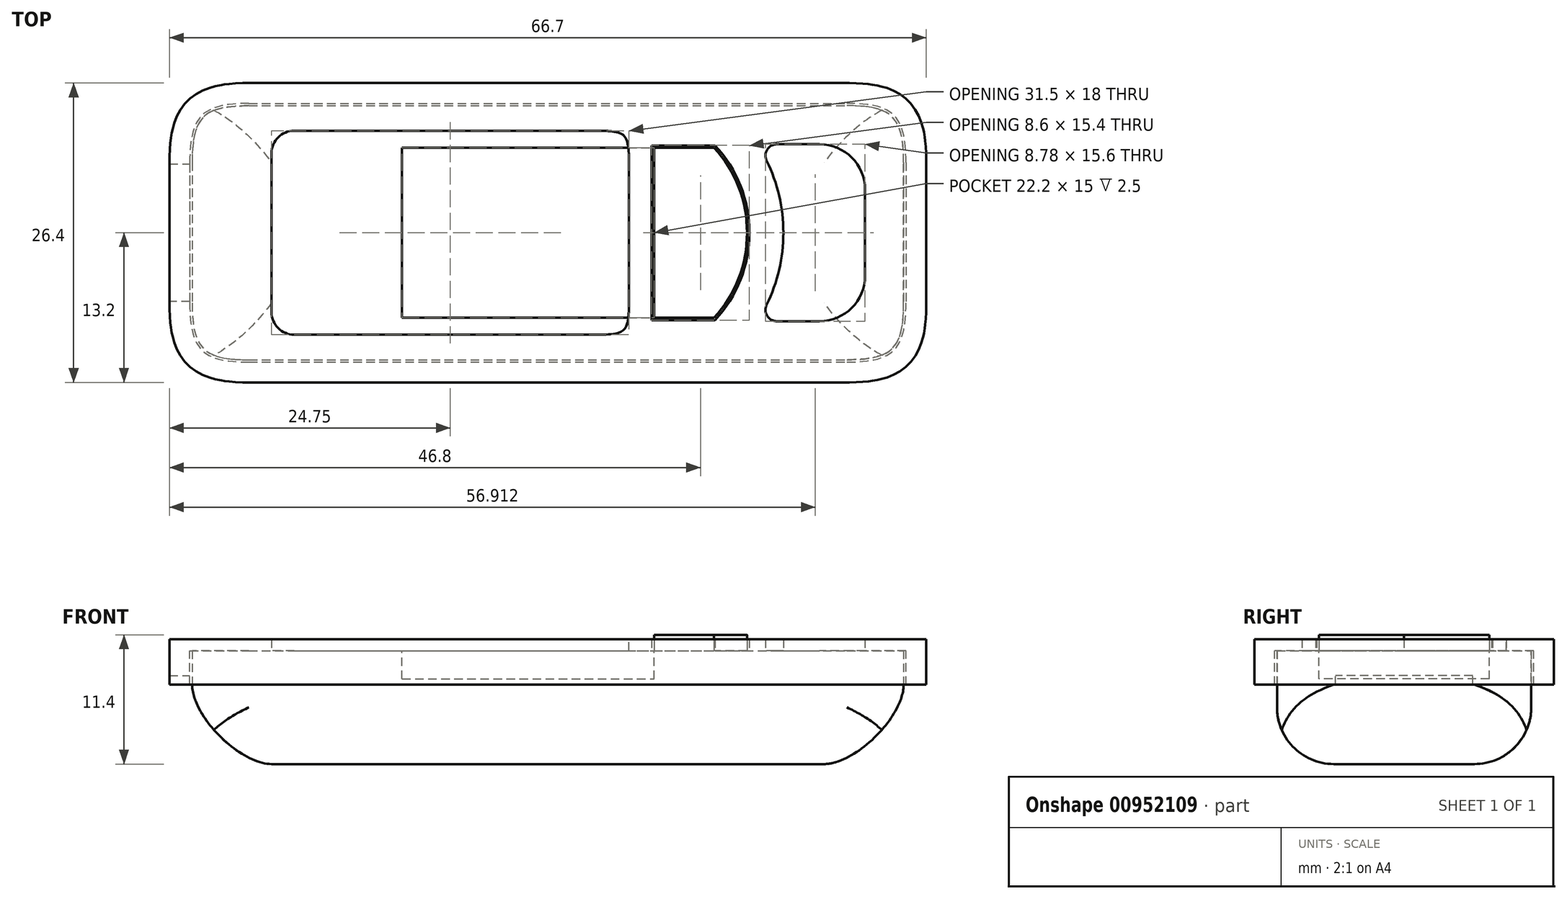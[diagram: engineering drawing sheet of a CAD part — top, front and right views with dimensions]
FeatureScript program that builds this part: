
annotation { "Feature Type Name" : "Feature", "Feature Type Description" : "" }
export const myFeature = defineFeature(function(context is Context, id is Id, definition is map)
    precondition{}
    {
        {
            var Q0;
            Q0=qCreatedBy(makeId("Top.planeOp"),FACE);
            var sketch = newSketch(context, id + "F0", { "sketchPlane" : qUnion([Q0])});
            skLineSegment(sketch, "E0.bottom", {"start": v(-27.35, 11.2) * mm, "end": v(27.35, 11.2) * mm});
            skLineSegment(sketch, "E0.top", {"start": v(-27.35, -11.2) * mm, "end": v(27.35, -11.2) * mm});
            skLineSegment(sketch, "E0.left", {"start": v(-31.35, 7.2) * mm, "end": v(-31.35, -7.2) * mm});
            skLineSegment(sketch, "E0.right", {"start": v(31.35, 7.2) * mm, "end": v(31.35, -7.2) * mm});
            skPoint(sketch, "E0.middle", {"position": v(0, 0) * mm});
            skLineSegment(sketch, "E1", {"start": v(31.35, 0) * mm, "end": v(17.55, 0) * mm, "construction": true});
            skLineSegment(sketch, "E2", {"start": v(17.55, 0) * mm, "end": v(9.35, 0) * mm, "construction": true});
            skLineSegment(sketch, "E3", {"start": v(9.35, 0) * mm, "end": v(-11.85, 0) * mm, "construction": true});
            skLineSegment(sketch, "E4", {"start": v(-11.85, 0) * mm, "end": v(-12.85, 0) * mm, "construction": true});
            skLineSegment(sketch, "E5", {"start": v(9.35, 0) * mm, "end": v(9.35, 7.5) * mm});
            skLineSegment(sketch, "E6.MirrorCS", {"start": v(9.35, 0) * mm, "end": v(9.35, -7.5) * mm});
            skLineSegment(sketch, "E7", {"start": v(9.35, 7.5) * mm, "end": v(14.65, 7.5) * mm});
            skLineSegment(sketch, "E8", {"start": v(14.65, 7.5) * mm, "end": v(14.65, 0) * mm});
            skArc(sketch, "E9", {"start": v(17.55, 0) * mm, "mid": v(16.8, 4.02) * mm, "end": v(14.65, 7.5) * mm});
            skLineSegment(sketch, "E10.MirrorCS", {"start": v(9.35, -7.5) * mm, "end": v(14.65, -7.5) * mm});
            skLineSegment(sketch, "E11.MirrorCS", {"start": v(14.65, -7.5) * mm, "end": v(14.65, 0) * mm});
            skArc(sketch, "E12.MirrorCS", {"start": v(17.55, 0) * mm, "mid": v(16.8, -4.02) * mm, "end": v(14.65, -7.5) * mm});
            skLineSegment(sketch, "E13", {"start": v(-12.85, 0) * mm, "end": v(-12.85, 7.5) * mm});
            skLineSegment(sketch, "E14", {"start": v(-12.85, 7.5) * mm, "end": v(9.35, 7.5) * mm});
            skLineSegment(sketch, "E15", {"start": v(-12.85, 0) * mm, "end": v(-12.85, -7.5) * mm});
            skLineSegment(sketch, "E16", {"start": v(-12.85, -7.5) * mm, "end": v(9.35, -7.5) * mm});
            skLineSegment(sketch, "E17", {"start": v(-31.35, 0) * mm, "end": v(-27.35, 0) * mm, "construction": true});
            skLineSegment(sketch, "E18", {"start": v(31.35, 0) * mm, "end": v(27.35, 0) * mm, "construction": true});
            skLineSegment(sketch, "E19", {"start": v(27.35, 0) * mm, "end": v(27.35, 11.2) * mm, "construction": true});
            skLineSegment(sketch, "E20", {"start": v(-27.35, 0) * mm, "end": v(-27.35, 11.2) * mm, "construction": true});
            skLineSegment(sketch, "E21.MirrorCS", {"start": v(-27.35, 0) * mm, "end": v(-27.35, -11.2) * mm, "construction": true});
            skLineSegment(sketch, "E22.MirrorCS", {"start": v(27.35, 0) * mm, "end": v(27.35, -11.2) * mm, "construction": true});
            skPoint(sketch, "E23.visualSharp", {"position": v(-31.35, 11.2) * mm});
            skArc(sketch, "E23.filletArc", {"start": v(-27.35, 11.2) * mm, "mid": v(-30.18, 10.03) * mm, "end": v(-31.35, 7.2) * mm});
            skPoint(sketch, "E24.visualSharp", {"position": v(-31.35, -11.2) * mm});
            skArc(sketch, "E24.filletArc", {"start": v(-31.35, -7.2) * mm, "mid": v(-30.18, -10.03) * mm, "end": v(-27.35, -11.2) * mm});
            skPoint(sketch, "E25.visualSharp", {"position": v(31.35, 11.2) * mm});
            skArc(sketch, "E25.filletArc", {"start": v(31.35, 7.2) * mm, "mid": v(30.18, 10.03) * mm, "end": v(27.35, 11.2) * mm});
            skPoint(sketch, "E26.visualSharp", {"position": v(31.35, -11.2) * mm});
            skArc(sketch, "E26.filletArc", {"start": v(27.35, -11.2) * mm, "mid": v(30.18, -10.03) * mm, "end": v(31.35, -7.2) * mm});
            skLineSegment(sketch, "E27", {"start": v(-27.35, 11.2) * mm, "end": v(-31.35, 11.2) * mm});
            skLineSegment(sketch, "E28", {"start": v(-31.35, 7.2) * mm, "end": v(-31.35, 11.2) * mm});
            skLineSegment(sketch, "E29.MirrorCS", {"start": v(-31.35, -7.2) * mm, "end": v(-31.35, -11.2) * mm});
            skLineSegment(sketch, "E30.MirrorCS", {"start": v(-27.35, -11.2) * mm, "end": v(-31.35, -11.2) * mm});
            skLineSegment(sketch, "E31.MirrorCS", {"start": v(27.35, 11.2) * mm, "end": v(31.35, 11.2) * mm});
            skLineSegment(sketch, "E32.MirrorCS", {"start": v(31.35, 7.2) * mm, "end": v(31.35, 11.2) * mm});
            skLineSegment(sketch, "E33.MirrorCS", {"start": v(27.35, -11.2) * mm, "end": v(31.35, -11.2) * mm});
            skLineSegment(sketch, "E34.MirrorCS", {"start": v(31.35, -7.2) * mm, "end": v(31.35, -11.2) * mm});
            skSolve(sketch);
        }
        {
            var Q0;
            Q0=makeQuery(id+"F0.imprint","IMPRINT",FACE,{"disambiguationData":[TD([[makeQuery(id+"F0.imprint","IMPRINT",EDGE,{"derivedFrom":sQuery(id+"F0.wireOp",EDGE,"E0.bottom")}),-1.0]])]});
            var Q1;
            Q1=makeQuery(id+"F0.imprint","IMPRINT",FACE,{"disambiguationData":[TD([[makeQuery(id+"F0.imprint","IMPRINT",EDGE,{"derivedFrom":sQuery(id+"F0.wireOp",EDGE,"E5")}),1.0]])]});
            var Q2;
            Q2=makeQuery(id+"F0.imprint","IMPRINT",FACE,{"disambiguationData":[TD([[makeQuery(id+"F0.imprint","IMPRINT",EDGE,{"derivedFrom":sQuery(id+"F0.wireOp",EDGE,"E5")}),-1.0]])]});
            var Q3;
            Q3=makeQuery(id+"F0.imprint","IMPRINT",FACE,{"disambiguationData":[TD([[makeQuery(id+"F0.imprint","IMPRINT",EDGE,{"derivedFrom":sQuery(id+"F0.wireOp",EDGE,"E8")}),1.0]])]});
            var Q4;
            Q4=makeQuery(id+"F0.imprint","IMPRINT",FACE,{"disambiguationData":[TD([[makeQuery(id+"F0.imprint","IMPRINT",EDGE,{"derivedFrom":sQuery(id+"F0.wireOp",EDGE,"E23.filletArc")}),-1.0]])]});
            var Q5;
            Q5=makeQuery(id+"F0.imprint","IMPRINT",FACE,{"disambiguationData":[TD([[makeQuery(id+"F0.imprint","IMPRINT",EDGE,{"derivedFrom":sQuery(id+"F0.wireOp",EDGE,"E24.filletArc")}),-1.0]])]});
            var Q6;
            Q6=makeQuery(id+"F0.imprint","IMPRINT",FACE,{"disambiguationData":[TD([[makeQuery(id+"F0.imprint","IMPRINT",EDGE,{"derivedFrom":sQuery(id+"F0.wireOp",EDGE,"E26.filletArc")}),-1.0]])]});
            var Q7;
            Q7=makeQuery(id+"F0.imprint","IMPRINT",FACE,{"disambiguationData":[TD([[makeQuery(id+"F0.imprint","IMPRINT",EDGE,{"derivedFrom":sQuery(id+"F0.wireOp",EDGE,"E25.filletArc")}),-1.0]])]});
            extrude(context, id + "F1", {"entities" : qUnion([Q0, Q1, Q2, Q3, Q4, Q5, Q6, Q7]), "oppositeDirection" : true, "depth" : 10 * mm, "offsetDistance" : 25 * mm});
        }
        {
            var Q0;
            Q0=makeQuery(id+"F0.imprint","IMPRINT",FACE,{"disambiguationData":[TD([[makeQuery(id+"F0.imprint","IMPRINT",EDGE,{"derivedFrom":sQuery(id+"F0.wireOp",EDGE,"E5")}),1.0]])]});
            extrude(context, id + "F2", {"entities" : qUnion([Q0]), "operationType" : NewBodyOperationType.REMOVE, "oppositeDirection" : true, "depth" : 2.5 * mm, "offsetDistance" : 25 * mm});
        }
        {
            var Q0;
            Q0=makeQuery(id+"F0.imprint","IMPRINT",FACE,{"disambiguationData":[TD([[makeQuery(id+"F0.imprint","IMPRINT",EDGE,{"derivedFrom":sQuery(id+"F0.wireOp",EDGE,"E5")}),-1.0]])]});
            var Q1;
            Q1=makeQuery(id+"F0.imprint","IMPRINT",FACE,{"disambiguationData":[TD([[makeQuery(id+"F0.imprint","IMPRINT",EDGE,{"derivedFrom":sQuery(id+"F0.wireOp",EDGE,"E8")}),1.0]])]});
            extrude(context, id + "F3", {"entities" : qUnion([Q0, Q1]), "operationType" : NewBodyOperationType.ADD, "depth" : 1.4 * mm, "offsetDistance" : 25 * mm});
        }
        {
            var Q0;
            Q0=makeQuery(id+"F1.opExtrude","SWEPT_EDGE",EDGE,{"disambiguationData":[OSD([sQuery(id+"F0.wireOp",EDGE,"E33.MirrorCS"),sQuery(id+"F0.wireOp",EDGE,"E34.MirrorCS")])]});
            var Q1;
            Q1=makeQuery(id+"F1.opExtrude","SWEPT_EDGE",EDGE,{"disambiguationData":[OSD([sQuery(id+"F0.wireOp",EDGE,"E31.MirrorCS"),sQuery(id+"F0.wireOp",EDGE,"E32.MirrorCS")])]});
            var Q2;
            Q2=makeQuery(id+"F1.opExtrude","SWEPT_EDGE",EDGE,{"disambiguationData":[OSD([sQuery(id+"F0.wireOp",EDGE,"E27"),sQuery(id+"F0.wireOp",EDGE,"E28")])]});
            var Q3;
            Q3=makeQuery(id+"F1.opExtrude","SWEPT_EDGE",EDGE,{"disambiguationData":[OSD([sQuery(id+"F0.wireOp",EDGE,"E29.MirrorCS"),sQuery(id+"F0.wireOp",EDGE,"E30.MirrorCS")])]});
            fillet(context, id + "F4", {"entities" : qUnion([Q0, Q1, Q2, Q3]), "radius" : 5 * mm, "rho" : .6, "crossSection" : FilletCrossSection.CONIC, "allowEdgeOverflow" : false});
        }
        {
            var Q0;
            Q0=makeQuery(id+"F1.opExtrude","CAP_EDGE",EDGE,{"disambiguationData":[OSD([sQuery(id+"F0.wireOp",EDGE,"E0.right"),sQuery(id+"F0.wireOp",EDGE,"E32.MirrorCS"),sQuery(id+"F0.wireOp",EDGE,"E34.MirrorCS")])],"isStart":false});
            var Q1;
            Q1=makeQuery(id+"F1.opExtrude","CAP_EDGE",EDGE,{"disambiguationData":[OSD([sQuery(id+"F0.wireOp",EDGE,"E0.left"),sQuery(id+"F0.wireOp",EDGE,"E28"),sQuery(id+"F0.wireOp",EDGE,"E29.MirrorCS")])],"isStart":false});
            fillet(context, id + "F5", {"entities" : qUnion([Q0, Q1]), "radius" : 7 * mm, "rho" : .3, "crossSection" : FilletCrossSection.CONIC, "allowEdgeOverflow" : false});
        }
        {
            var Q0;
            Q0=makeQuery(id+"F1.opExtrude","CAP_EDGE",EDGE,{"disambiguationData":[OSD([sQuery(id+"F0.wireOp",EDGE,"E0.bottom"),sQuery(id+"F0.wireOp",EDGE,"E27"),sQuery(id+"F0.wireOp",EDGE,"E31.MirrorCS")])],"isStart":false});
            var Q1;
            Q1=makeQuery(id+"F1.opExtrude","CAP_EDGE",EDGE,{"disambiguationData":[OSD([sQuery(id+"F0.wireOp",EDGE,"E0.top"),sQuery(id+"F0.wireOp",EDGE,"E30.MirrorCS"),sQuery(id+"F0.wireOp",EDGE,"E33.MirrorCS")])],"isStart":false});
            fillet(context, id + "F6", {"entities" : qUnion([Q0, Q1]), "radius" : 5 * mm, "allowEdgeOverflow" : false});
        }
        {
            var Q0;
            Q0=makeQuery(id+"F1.opExtrude","CAP_FACE",FACE,{"disambiguationData":[OSD([sQuery(id+"F0.wireOp",EDGE,"E0.bottom"),sQuery(id+"F0.wireOp",EDGE,"E0.top"),sQuery(id+"F0.wireOp",EDGE,"E0.left"),sQuery(id+"F0.wireOp",EDGE,"E0.right"),sQuery(id+"F0.wireOp",EDGE,"E27"),sQuery(id+"F0.wireOp",EDGE,"E28"),sQuery(id+"F0.wireOp",EDGE,"E29.MirrorCS"),sQuery(id+"F0.wireOp",EDGE,"E30.MirrorCS"),sQuery(id+"F0.wireOp",EDGE,"E31.MirrorCS"),sQuery(id+"F0.wireOp",EDGE,"E32.MirrorCS"),sQuery(id+"F0.wireOp",EDGE,"E33.MirrorCS"),sQuery(id+"F0.wireOp",EDGE,"E34.MirrorCS")])],"isStart":true});
            var sketch = newSketch(context, id + "F7", { "sketchPlane" : qUnion([Q0])});
            skFitSpline(sketch, "E35.0", {"points": [v(-26.35, 13.2) * mm, v(-26.58, 13.2) * mm, v(-26.91, 13.2) * mm, v(-27.34, 13.18) * mm, v(-27.65, 13.16) * mm, v(-27.95, 13.14) * mm, v(-28.2, 13.1) * mm, v(-28.38, 13.09) * mm, v(-28.5, 13.07) * mm, v(-28.6, 13.06) * mm, v(-28.66, 13.05) * mm, v(-28.72, 13.04) * mm, v(-28.76, 13.03) * mm, v(-28.78, 13.03) * mm, v(-28.8, 13.02) * mm, v(-28.83, 13.02) * mm, v(-28.86, 13.01) * mm, v(-28.92, 13) * mm, v(-29, 12.98) * mm, v(-29.1, 12.96) * mm, v(-29.24, 12.93) * mm, v(-29.41, 12.9) * mm, v(-29.68, 12.82) * mm, v(-30, 12.71) * mm, v(-30.39, 12.56) * mm, v(-30.76, 12.37) * mm, v(-31.12, 12.15) * mm, v(-31.46, 11.9) * mm, v(-31.78, 11.61) * mm, v(-32.06, 11.3) * mm, v(-32.31, 10.95) * mm, v(-32.53, 10.6) * mm, v(-32.71, 10.23) * mm, v(-32.86, 9.85) * mm, v(-32.97, 9.52) * mm, v(-33.04, 9.26) * mm, v(-33.08, 9.09) * mm, v(-33.11, 8.95) * mm, v(-33.14, 8.85) * mm, v(-33.15, 8.77) * mm, v(-33.16, 8.7) * mm, v(-33.17, 8.67) * mm, v(-33.17, 8.64) * mm, v(-33.18, 8.63) * mm, v(-33.18, 8.6) * mm, v(-33.19, 8.57) * mm, v(-33.2, 8.5) * mm, v(-33.2, 8.44) * mm, v(-33.22, 8.35) * mm, v(-33.24, 8.23) * mm, v(-33.26, 8.04) * mm, v(-33.29, 7.8) * mm, v(-33.3, 7.5) * mm, v(-33.33, 7.19) * mm, v(-33.35, 6.76) * mm, v(-33.35, 6.43) * mm, v(-33.35, 6.2) * mm]});
            skLineSegment(sketch, "E35.1", {"start": v(-33.35, 6.2) * mm, "end": v(-33.35, -6.2) * mm});
            skLineSegment(sketch, "E35.2", {"start": v(-26.35, 13.2) * mm, "end": v(26.35, 13.2) * mm});
            skFitSpline(sketch, "E35.3", {"points": [v(-33.35, -6.2) * mm, v(-33.35, -6.43) * mm, v(-33.34, -6.76) * mm, v(-33.33, -7.19) * mm, v(-33.3, -7.5) * mm, v(-33.29, -7.8) * mm, v(-33.26, -8.04) * mm, v(-33.24, -8.23) * mm, v(-33.22, -8.35) * mm, v(-33.2, -8.44) * mm, v(-33.2, -8.51) * mm, v(-33.19, -8.57) * mm, v(-33.18, -8.61) * mm, v(-33.18, -8.63) * mm, v(-33.17, -8.65) * mm, v(-33.17, -8.68) * mm, v(-33.16, -8.71) * mm, v(-33.15, -8.77) * mm, v(-33.13, -8.86) * mm, v(-33.11, -8.96) * mm, v(-33.08, -9.1) * mm, v(-33.04, -9.26) * mm, v(-32.97, -9.53) * mm, v(-32.86, -9.86) * mm, v(-32.7, -10.24) * mm, v(-32.52, -10.6) * mm, v(-32.3, -10.97) * mm, v(-32.05, -11.3) * mm, v(-31.76, -11.63) * mm, v(-31.44, -11.91) * mm, v(-31.1, -12.16) * mm, v(-30.75, -12.38) * mm, v(-30.38, -12.56) * mm, v(-30, -12.71) * mm, v(-29.67, -12.82) * mm, v(-29.4, -12.9) * mm, v(-29.24, -12.93) * mm, v(-29.1, -12.96) * mm, v(-29, -12.99) * mm, v(-28.92, -13) * mm, v(-28.86, -13.01) * mm, v(-28.82, -13.02) * mm, v(-28.8, -13.02) * mm, v(-28.78, -13.03) * mm, v(-28.75, -13.03) * mm, v(-28.72, -13.04) * mm, v(-28.66, -13.05) * mm, v(-28.59, -13.06) * mm, v(-28.5, -13.07) * mm, v(-28.38, -13.09) * mm, v(-28.19, -13.11) * mm, v(-27.95, -13.14) * mm, v(-27.65, -13.16) * mm, v(-27.34, -13.18) * mm, v(-26.91, -13.2) * mm, v(-26.58, -13.2) * mm, v(-26.35, -13.2) * mm]});
            skFitSpline(sketch, "E35.4", {"points": [v(33.35, 6.2) * mm, v(33.35, 6.43) * mm, v(33.34, 6.76) * mm, v(33.33, 7.19) * mm, v(33.3, 7.5) * mm, v(33.29, 7.8) * mm, v(33.26, 8.04) * mm, v(33.24, 8.23) * mm, v(33.22, 8.35) * mm, v(33.2, 8.44) * mm, v(33.2, 8.51) * mm, v(33.19, 8.57) * mm, v(33.18, 8.61) * mm, v(33.18, 8.63) * mm, v(33.17, 8.65) * mm, v(33.17, 8.68) * mm, v(33.16, 8.71) * mm, v(33.15, 8.77) * mm, v(33.13, 8.86) * mm, v(33.11, 8.96) * mm, v(33.08, 9.1) * mm, v(33.04, 9.26) * mm, v(32.97, 9.53) * mm, v(32.86, 9.86) * mm, v(32.7, 10.24) * mm, v(32.52, 10.6) * mm, v(32.3, 10.97) * mm, v(32.05, 11.3) * mm, v(31.76, 11.63) * mm, v(31.44, 11.91) * mm, v(31.1, 12.16) * mm, v(30.75, 12.38) * mm, v(30.38, 12.56) * mm, v(30, 12.71) * mm, v(29.67, 12.82) * mm, v(29.4, 12.9) * mm, v(29.24, 12.93) * mm, v(29.1, 12.96) * mm, v(29, 12.99) * mm, v(28.92, 13) * mm, v(28.86, 13.01) * mm, v(28.82, 13.02) * mm, v(28.8, 13.02) * mm, v(28.78, 13.03) * mm, v(28.75, 13.03) * mm, v(28.72, 13.04) * mm, v(28.66, 13.05) * mm, v(28.59, 13.06) * mm, v(28.5, 13.07) * mm, v(28.38, 13.09) * mm, v(28.19, 13.11) * mm, v(27.95, 13.14) * mm, v(27.65, 13.16) * mm, v(27.34, 13.18) * mm, v(26.91, 13.2) * mm, v(26.58, 13.2) * mm, v(26.35, 13.2) * mm]});
            skLineSegment(sketch, "E35.5", {"start": v(33.35, 6.2) * mm, "end": v(33.35, -6.2) * mm});
            skFitSpline(sketch, "E35.6", {"points": [v(26.35, -13.2) * mm, v(26.58, -13.2) * mm, v(26.91, -13.2) * mm, v(27.34, -13.18) * mm, v(27.65, -13.16) * mm, v(27.95, -13.14) * mm, v(28.2, -13.1) * mm, v(28.38, -13.09) * mm, v(28.5, -13.07) * mm, v(28.6, -13.06) * mm, v(28.66, -13.05) * mm, v(28.72, -13.04) * mm, v(28.76, -13.03) * mm, v(28.78, -13.03) * mm, v(28.8, -13.02) * mm, v(28.83, -13.02) * mm, v(28.86, -13.01) * mm, v(28.92, -13) * mm, v(29, -12.98) * mm, v(29.1, -12.96) * mm, v(29.24, -12.93) * mm, v(29.41, -12.9) * mm, v(29.68, -12.82) * mm, v(30, -12.71) * mm, v(30.39, -12.56) * mm, v(30.76, -12.37) * mm, v(31.12, -12.15) * mm, v(31.46, -11.9) * mm, v(31.78, -11.61) * mm, v(32.06, -11.3) * mm, v(32.31, -10.95) * mm, v(32.53, -10.6) * mm, v(32.71, -10.23) * mm, v(32.86, -9.85) * mm, v(32.97, -9.52) * mm, v(33.04, -9.26) * mm, v(33.08, -9.09) * mm, v(33.11, -8.95) * mm, v(33.14, -8.85) * mm, v(33.15, -8.77) * mm, v(33.16, -8.7) * mm, v(33.17, -8.67) * mm, v(33.17, -8.64) * mm, v(33.18, -8.63) * mm, v(33.18, -8.6) * mm, v(33.19, -8.57) * mm, v(33.2, -8.5) * mm, v(33.2, -8.44) * mm, v(33.22, -8.35) * mm, v(33.24, -8.23) * mm, v(33.26, -8.04) * mm, v(33.29, -7.8) * mm, v(33.3, -7.5) * mm, v(33.33, -7.19) * mm, v(33.35, -6.76) * mm, v(33.35, -6.43) * mm, v(33.35, -6.2) * mm]});
            skLineSegment(sketch, "E35.7", {"start": v(-26.35, -13.2) * mm, "end": v(26.35, -13.2) * mm});
            skLineSegment(sketch, "E36.0", {"start": v(9.15, 7.7) * mm, "end": v(14.74, 7.7) * mm});
            skLineSegment(sketch, "E36.1", {"start": v(9.15, -7.7) * mm, "end": v(9.15, 7.7) * mm});
            skArc(sketch, "E36.2", {"start": v(17.75, 0) * mm, "mid": v(16.98, 4.14) * mm, "end": v(14.74, 7.7) * mm});
            skArc(sketch, "E36.3", {"start": v(17.75, 0) * mm, "mid": v(16.98, -4.14) * mm, "end": v(14.74, -7.7) * mm});
            skLineSegment(sketch, "E36.4", {"start": v(9.15, -7.7) * mm, "end": v(14.74, -7.7) * mm});
            skLineSegment(sketch, "E37", {"start": v(9.15, 7.7) * mm, "end": v(9.15, 11.2) * mm});
            skLineSegment(sketch, "E38", {"start": v(-31.35, 0) * mm, "end": v(31.35, 0) * mm, "construction": true});
            skLineSegment(sketch, "E39", {"start": v(9.15, -7.79) * mm, "end": v(9.15, -11.2) * mm});
            skLineSegment(sketch, "E40", {"start": v(9.15, 0) * mm, "end": v(7.15, 0) * mm});
            skLineSegment(sketch, "E41", {"start": v(7.15, 0) * mm, "end": v(7.15, 11.2) * mm});
            skLineSegment(sketch, "E42.MirrorCS", {"start": v(7.15, 0) * mm, "end": v(7.15, -11.2) * mm});
            skLineSegment(sketch, "E43.0", {"start": v(-14.35, 9) * mm, "end": v(9.15, 9) * mm});
            skLineSegment(sketch, "E43.1", {"start": v(-14.35, 9) * mm, "end": v(-14.35, -9) * mm});
            skLineSegment(sketch, "E43.2", {"start": v(-14.35, -9) * mm, "end": v(9.15, -9) * mm});
            skLineSegment(sketch, "E44", {"start": v(-14.35, 9) * mm, "end": v(-24.35, 9) * mm});
            skLineSegment(sketch, "E45", {"start": v(-24.35, 9) * mm, "end": v(-24.35, -9) * mm});
            skLineSegment(sketch, "E46", {"start": v(-24.35, -9) * mm, "end": v(-14.35, -9) * mm});
            skLineSegment(sketch, "E47", {"start": v(26.35, 13.2) * mm, "end": v(33.35, 13.2) * mm});
            skLineSegment(sketch, "E48", {"start": v(33.35, 13.2) * mm, "end": v(33.35, 6.2) * mm});
            skLineSegment(sketch, "E49", {"start": v(33.35, -6.2) * mm, "end": v(33.35, -13.2) * mm});
            skLineSegment(sketch, "E50", {"start": v(33.35, -13.2) * mm, "end": v(26.35, -13.2) * mm});
            skLineSegment(sketch, "E51.0", {"start": v(20.17, -7.8) * mm, "end": v(23.95, -7.8) * mm});
            skLineSegment(sketch, "E51.1", {"start": v(27.95, -7.8) * mm, "end": v(26.35, -7.8) * mm});
            skLineSegment(sketch, "E51.2", {"start": v(27.95, -6.2) * mm, "end": v(27.95, -7.8) * mm});
            skLineSegment(sketch, "E51.3", {"start": v(20.17, 7.8) * mm, "end": v(23.95, 7.8) * mm});
            skLineSegment(sketch, "E51.4", {"start": v(26.35, 7.8) * mm, "end": v(27.95, 7.8) * mm});
            skLineSegment(sketch, "E51.5", {"start": v(27.95, 7.8) * mm, "end": v(27.95, 6.2) * mm});
            skLineSegment(sketch, "E51.6", {"start": v(27.95, 3.8) * mm, "end": v(27.95, -3.8) * mm});
            skArc(sketch, "E52.0", {"start": v(20.75, 0) * mm, "mid": v(20.38, 3.26) * mm, "end": v(19.28, 6.36) * mm});
            skArc(sketch, "E52.1", {"start": v(20.75, 0) * mm, "mid": v(20.38, -3.26) * mm, "end": v(19.28, -6.36) * mm});
            skArc(sketch, "E53.filletArc", {"start": v(27.95, 3.8) * mm, "mid": v(26.78, 6.63) * mm, "end": v(23.95, 7.8) * mm});
            skArc(sketch, "E54.filletArc", {"start": v(23.95, -7.8) * mm, "mid": v(26.78, -6.63) * mm, "end": v(27.95, -3.8) * mm});
            skArc(sketch, "E55.filletArc", {"start": v(20.17, 7.8) * mm, "mid": v(19.32, 7.33) * mm, "end": v(19.28, 6.36) * mm});
            skArc(sketch, "E56.filletArc", {"start": v(19.28, -6.36) * mm, "mid": v(19.32, -7.33) * mm, "end": v(20.17, -7.8) * mm});
            skFitSpline(sketch, "E57.0", {"points": [v(-31.55, -6.2) * mm, v(-31.55, -6.41) * mm, v(-31.55, -6.72) * mm, v(-31.53, -7.1) * mm, v(-31.51, -7.37) * mm, v(-31.5, -7.64) * mm, v(-31.47, -7.84) * mm, v(-31.45, -8) * mm, v(-31.44, -8.1) * mm, v(-31.43, -8.17) * mm, v(-31.42, -8.23) * mm, v(-31.41, -8.28) * mm, v(-31.4, -8.3) * mm, v(-31.4, -8.33) * mm, v(-31.4, -8.34) * mm, v(-31.4, -8.36) * mm, v(-31.4, -8.39) * mm, v(-31.38, -8.43) * mm, v(-31.37, -8.5) * mm, v(-31.35, -8.58) * mm, v(-31.33, -8.68) * mm, v(-31.3, -8.8) * mm, v(-31.25, -9) * mm, v(-31.17, -9.24) * mm, v(-31.06, -9.5) * mm, v(-30.94, -9.74) * mm, v(-30.76, -10.04) * mm, v(-30.5, -10.36) * mm, v(-30.18, -10.62) * mm, v(-29.88, -10.8) * mm, v(-29.64, -10.92) * mm, v(-29.38, -11.02) * mm, v(-29.15, -11.1) * mm, v(-28.95, -11.15) * mm, v(-28.83, -11.18) * mm, v(-28.72, -11.2) * mm, v(-28.65, -11.22) * mm, v(-28.58, -11.23) * mm, v(-28.53, -11.24) * mm, v(-28.5, -11.25) * mm, v(-28.48, -11.25) * mm, v(-28.47, -11.25) * mm, v(-28.45, -11.26) * mm, v(-28.42, -11.26) * mm, v(-28.38, -11.27) * mm, v(-28.32, -11.28) * mm, v(-28.24, -11.29) * mm, v(-28.15, -11.3) * mm, v(-27.99, -11.32) * mm, v(-27.78, -11.34) * mm, v(-27.52, -11.36) * mm, v(-27.25, -11.38) * mm, v(-26.87, -11.4) * mm, v(-26.56, -11.4) * mm, v(-26.35, -11.4) * mm]});
            skLineSegment(sketch, "E57.1", {"start": v(-31.55, 6.2) * mm, "end": v(-31.55, -6.2) * mm});
            skLineSegment(sketch, "E57.2", {"start": v(-26.35, -11.4) * mm, "end": v(26.35, -11.4) * mm});
            skFitSpline(sketch, "E57.3", {"points": [v(-26.35, 11.4) * mm, v(-26.56, 11.4) * mm, v(-26.87, 11.4) * mm, v(-27.25, 11.38) * mm, v(-27.52, 11.36) * mm, v(-27.79, 11.34) * mm, v(-28, 11.32) * mm, v(-28.15, 11.3) * mm, v(-28.25, 11.29) * mm, v(-28.32, 11.28) * mm, v(-28.38, 11.27) * mm, v(-28.43, 11.26) * mm, v(-28.46, 11.26) * mm, v(-28.48, 11.25) * mm, v(-28.49, 11.25) * mm, v(-28.51, 11.25) * mm, v(-28.54, 11.24) * mm, v(-28.58, 11.23) * mm, v(-28.65, 11.22) * mm, v(-28.73, 11.2) * mm, v(-28.83, 11.18) * mm, v(-28.96, 11.15) * mm, v(-29.15, 11.1) * mm, v(-29.39, 11.02) * mm, v(-29.65, 10.91) * mm, v(-29.89, 10.8) * mm, v(-30.19, 10.61) * mm, v(-30.5, 10.35) * mm, v(-30.77, 10.03) * mm, v(-30.95, 9.73) * mm, v(-31.07, 9.5) * mm, v(-31.17, 9.23) * mm, v(-31.25, 9) * mm, v(-31.3, 8.8) * mm, v(-31.33, 8.68) * mm, v(-31.35, 8.57) * mm, v(-31.37, 8.5) * mm, v(-31.38, 8.43) * mm, v(-31.4, 8.38) * mm, v(-31.4, 8.36) * mm, v(-31.4, 8.33) * mm, v(-31.4, 8.32) * mm, v(-31.4, 8.3) * mm, v(-31.41, 8.27) * mm, v(-31.42, 8.23) * mm, v(-31.43, 8.17) * mm, v(-31.44, 8.1) * mm, v(-31.45, 8) * mm, v(-31.47, 7.84) * mm, v(-31.5, 7.63) * mm, v(-31.51, 7.37) * mm, v(-31.53, 7.1) * mm, v(-31.55, 6.72) * mm, v(-31.55, 6.41) * mm, v(-31.55, 6.2) * mm]});
            skFitSpline(sketch, "E57.4", {"points": [v(26.35, -11.4) * mm, v(26.56, -11.4) * mm, v(26.87, -11.4) * mm, v(27.25, -11.38) * mm, v(27.52, -11.36) * mm, v(27.79, -11.34) * mm, v(28, -11.32) * mm, v(28.15, -11.3) * mm, v(28.25, -11.29) * mm, v(28.32, -11.28) * mm, v(28.38, -11.27) * mm, v(28.43, -11.26) * mm, v(28.46, -11.26) * mm, v(28.48, -11.25) * mm, v(28.49, -11.25) * mm, v(28.51, -11.25) * mm, v(28.54, -11.24) * mm, v(28.58, -11.23) * mm, v(28.65, -11.22) * mm, v(28.73, -11.2) * mm, v(28.83, -11.18) * mm, v(28.96, -11.15) * mm, v(29.15, -11.1) * mm, v(29.39, -11.02) * mm, v(29.65, -10.91) * mm, v(29.89, -10.8) * mm, v(30.19, -10.61) * mm, v(30.5, -10.35) * mm, v(30.77, -10.03) * mm, v(30.95, -9.73) * mm, v(31.07, -9.5) * mm, v(31.17, -9.23) * mm, v(31.25, -9) * mm, v(31.3, -8.8) * mm, v(31.33, -8.68) * mm, v(31.35, -8.57) * mm, v(31.37, -8.5) * mm, v(31.38, -8.43) * mm, v(31.4, -8.38) * mm, v(31.4, -8.36) * mm, v(31.4, -8.33) * mm, v(31.4, -8.32) * mm, v(31.4, -8.3) * mm, v(31.41, -8.27) * mm, v(31.42, -8.23) * mm, v(31.43, -8.17) * mm, v(31.44, -8.1) * mm, v(31.45, -8) * mm, v(31.47, -7.84) * mm, v(31.5, -7.63) * mm, v(31.51, -7.37) * mm, v(31.53, -7.1) * mm, v(31.55, -6.72) * mm, v(31.55, -6.41) * mm, v(31.55, -6.2) * mm]});
            skLineSegment(sketch, "E57.5", {"start": v(31.55, 6.2) * mm, "end": v(31.55, -6.2) * mm});
            skFitSpline(sketch, "E57.6", {"points": [v(31.55, 6.2) * mm, v(31.55, 6.41) * mm, v(31.55, 6.72) * mm, v(31.53, 7.1) * mm, v(31.51, 7.37) * mm, v(31.5, 7.64) * mm, v(31.47, 7.84) * mm, v(31.45, 8) * mm, v(31.44, 8.1) * mm, v(31.43, 8.17) * mm, v(31.42, 8.23) * mm, v(31.41, 8.28) * mm, v(31.4, 8.3) * mm, v(31.4, 8.33) * mm, v(31.4, 8.34) * mm, v(31.4, 8.36) * mm, v(31.4, 8.39) * mm, v(31.38, 8.43) * mm, v(31.37, 8.5) * mm, v(31.35, 8.58) * mm, v(31.33, 8.68) * mm, v(31.3, 8.8) * mm, v(31.25, 9) * mm, v(31.17, 9.24) * mm, v(31.06, 9.5) * mm, v(30.94, 9.74) * mm, v(30.76, 10.04) * mm, v(30.5, 10.36) * mm, v(30.18, 10.62) * mm, v(29.88, 10.8) * mm, v(29.64, 10.92) * mm, v(29.38, 11.02) * mm, v(29.15, 11.1) * mm, v(28.95, 11.15) * mm, v(28.83, 11.18) * mm, v(28.72, 11.2) * mm, v(28.65, 11.22) * mm, v(28.58, 11.23) * mm, v(28.53, 11.24) * mm, v(28.5, 11.25) * mm, v(28.48, 11.25) * mm, v(28.47, 11.25) * mm, v(28.45, 11.26) * mm, v(28.42, 11.26) * mm, v(28.38, 11.27) * mm, v(28.32, 11.28) * mm, v(28.24, 11.29) * mm, v(28.15, 11.3) * mm, v(27.99, 11.32) * mm, v(27.78, 11.34) * mm, v(27.52, 11.36) * mm, v(27.25, 11.38) * mm, v(26.87, 11.4) * mm, v(26.56, 11.4) * mm, v(26.35, 11.4) * mm]});
            skLineSegment(sketch, "E57.7", {"start": v(-26.35, 11.4) * mm, "end": v(26.35, 11.4) * mm});
            skLineSegment(sketch, "E58", {"start": v(-31.55, 0) * mm, "end": v(-33.35, 0) * mm, "construction": true});
            skLineSegment(sketch, "E59", {"start": v(-32.45, 0) * mm, "end": v(-32.45, 6.05) * mm, "construction": true});
            skLineSegment(sketch, "E60", {"start": v(-32.45, 6.05) * mm, "end": v(-31.35, 6.05) * mm});
            skLineSegment(sketch, "E61", {"start": v(-32.45, 6.05) * mm, "end": v(-33.35, 6.05) * mm});
            skLineSegment(sketch, "E62.MirrorCS", {"start": v(-32.45, 0) * mm, "end": v(-32.45, -6.05) * mm, "construction": true});
            skLineSegment(sketch, "E63.MirrorCS", {"start": v(-32.45, -6.05) * mm, "end": v(-33.35, -6.05) * mm});
            skLineSegment(sketch, "E64.MirrorCS", {"start": v(-32.45, -6.05) * mm, "end": v(-31.35, -6.05) * mm});
            skSolve(sketch);
        }
        {
            var Q0;
            Q0=makeQuery(id+"F7.imprint","IMPRINT",FACE,{"disambiguationData":[TD([[makeQuery(id+"F7.imprint","IMPRINT",EDGE,{"derivedFrom":sQuery(id+"F7.wireOp",EDGE,"E35.0")}),1.0]])]});
            var Q1;
            {var subQ11=sQuery(id+"F7.wireOp",EDGE,"E44");Q1=makeQuery(id+"F7.imprint","IMPRINT",FACE,{"disambiguationData":[TD([[makeQuery(id+"F7.imprint","IMPRINT",EDGE,{"derivedFrom":subQ11}),-1.0]])]});}
            var Q2;
            {var subQ0=sQuery(id+"F7.wireOp",EDGE,"E37");var subQ3=sQuery(id+"F7.wireOp",EDGE,"E43.0");var subQ4=makeQuery(id+"F7.imprint","INTERSECT",VERTEX,{"derivedFrom":[subQ0,subQ3]});Q2=makeQuery(id+"F7.imprint","IMPRINT",FACE,{"disambiguationData":[TD([[makeQuery(id+"F7.imprint","IMPRINT",EDGE,{"disambiguationData":[TD([[subQ4,1.0]])],"derivedFrom":subQ3}),1.0]])]});}
            var Q3;
            {var subQ21=sQuery(id+"F7.wireOp",EDGE,"E36.0");Q3=makeQuery(id+"F7.imprint","IMPRINT",FACE,{"disambiguationData":[TD([[makeQuery(id+"F7.imprint","IMPRINT",EDGE,{"derivedFrom":subQ21}),1.0]])]});}
            var Q4;
            {var subQ0=sQuery(id+"F7.wireOp",EDGE,"E43.0");var subQ1=sQuery(id+"F7.wireOp",EDGE,"E41");var subQ2=makeQuery(id+"F7.imprint","INTERSECT",VERTEX,{"derivedFrom":[subQ1,subQ0]});Q4=makeQuery(id+"F7.imprint","IMPRINT",FACE,{"disambiguationData":[TD([[makeQuery(id+"F7.imprint","IMPRINT",EDGE,{"disambiguationData":[TD([[subQ2,1.0]])],"derivedFrom":subQ1}),-1.0]])]});}
            var Q5;
            {var subQ0=sQuery(id+"F7.wireOp",EDGE,"E39");var subQ3=sQuery(id+"F7.wireOp",EDGE,"E43.2");var subQ4=makeQuery(id+"F7.imprint","INTERSECT",VERTEX,{"derivedFrom":[subQ0,subQ3]});Q5=makeQuery(id+"F7.imprint","IMPRINT",FACE,{"disambiguationData":[TD([[makeQuery(id+"F7.imprint","IMPRINT",EDGE,{"disambiguationData":[TD([[subQ4,1.0]])],"derivedFrom":subQ3}),-1.0]])]});}
            var Q6;
            {var subQ0=sQuery(id+"F7.wireOp",EDGE,"E40");Q6=makeQuery(id+"F7.imprint","IMPRINT",FACE,{"disambiguationData":[TD([[makeQuery(id+"F7.imprint","IMPRINT",EDGE,{"derivedFrom":subQ0}),-1.0]])]});}
            var Q7;
            {var subQ0=sQuery(id+"F7.wireOp",EDGE,"E40");Q7=makeQuery(id+"F7.imprint","IMPRINT",FACE,{"disambiguationData":[TD([[makeQuery(id+"F7.imprint","IMPRINT",EDGE,{"derivedFrom":subQ0}),1.0]])]});}
            var Q8;
            {var subQ0=sQuery(id+"F7.wireOp",EDGE,"E51.3");var subQ3=sQuery(id+"F7.wireOp",EDGE,"E41");var subQ4=makeQuery(id+"F7.imprint","INTERSECT",VERTEX,{"derivedFrom":[subQ3,subQ0]});Q8=makeQuery(id+"F7.imprint","IMPRINT",FACE,{"disambiguationData":[TD([[makeQuery(id+"F7.imprint","IMPRINT",EDGE,{"disambiguationData":[TD([[subQ4,1.0]])],"derivedFrom":subQ3}),-1.0]])]});}
            var Q9;
            {var subQ0=sQuery(id+"F7.wireOp",EDGE,"E43.2");var subQ1=sQuery(id+"F7.wireOp",EDGE,"E39");var subQ2=makeQuery(id+"F7.imprint","INTERSECT",VERTEX,{"derivedFrom":[subQ1,subQ0]});Q9=makeQuery(id+"F7.imprint","IMPRINT",FACE,{"disambiguationData":[TD([[makeQuery(id+"F7.imprint","IMPRINT",EDGE,{"disambiguationData":[TD([[subQ2,1.0]])],"derivedFrom":subQ1}),-1.0]])]});}
            var Q10;
            Q10=makeQuery(id+"F7.imprint","IMPRINT",FACE,{"disambiguationData":[TD([[makeQuery(id+"F7.imprint","IMPRINT",EDGE,{"derivedFrom":sQuery(id+"F7.wireOp",EDGE,"E51.6")}),1.0]])]});
            var Q11;
            Q11=makeQuery(id+"F7.imprint","IMPRINT",FACE,{"disambiguationData":[TD([[makeQuery(id+"F7.imprint","IMPRINT",EDGE,{"derivedFrom":sQuery(id+"F7.wireOp",EDGE,"E57.0")}),1.0]])]});
            var Q12;
            {var subQ0=sQuery(id+"F7.wireOp",EDGE,"E61");Q12=makeQuery(id+"F7.imprint","IMPRINT",FACE,{"disambiguationData":[TD([[makeQuery(id+"F7.imprint","IMPRINT",EDGE,{"derivedFrom":subQ0}),1.0]])]});}
            var Q13;
            {var subQ0=sQuery(id+"F7.wireOp",EDGE,"E60");var subQ1=sQuery(id+"F7.wireOp",EDGE,"E57.1");var subQ2=makeQuery(id+"F7.imprint","INTERSECT",VERTEX,{"derivedFrom":[subQ1,subQ0]});Q13=makeQuery(id+"F7.imprint","IMPRINT",FACE,{"disambiguationData":[TD([[makeQuery(id+"F7.imprint","IMPRINT",EDGE,{"disambiguationData":[TD([[subQ2,-1.0]])],"derivedFrom":subQ1}),1.0]])]});}
            extrude(context, id + "F8", {"entities" : qUnion([Q0, Q1, Q2, Q3, Q4, Q5, Q6, Q7, Q8, Q9, Q10, Q11, Q12, Q13]), "depth" : 1 * mm, "offsetDistance" : 25 * mm});
        }
        {
            var Q0;
            Q0=makeQuery(id+"F8.opExtrude","SWEPT_EDGE",EDGE,{"disambiguationData":[OSD([sQuery(id+"F7.wireOp",EDGE,"E41"),sQuery(id+"F7.wireOp",EDGE,"E43.0")])]});
            var Q1;
            Q1=makeQuery(id+"F8.opExtrude","SWEPT_EDGE",EDGE,{"disambiguationData":[OSD([sQuery(id+"F7.wireOp",EDGE,"E42.MirrorCS"),sQuery(id+"F7.wireOp",EDGE,"E43.2")])]});
            fillet(context, id + "F9", {"entities" : qUnion([Q0, Q1]), "radius" : 3 * mm, "tangentPropagation" : true, "rho" : .7, "crossSection" : FilletCrossSection.CONIC, "allowEdgeOverflow" : false});
        }
        {
            var Q0;
            Q0=makeQuery(id+"F8.opExtrude","SWEPT_EDGE",EDGE,{"disambiguationData":[OSD([sQuery(id+"F7.wireOp",EDGE,"E44"),sQuery(id+"F7.wireOp",EDGE,"E45")])]});
            var Q1;
            Q1=makeQuery(id+"F8.opExtrude","SWEPT_EDGE",EDGE,{"disambiguationData":[OSD([sQuery(id+"F7.wireOp",EDGE,"E45"),sQuery(id+"F7.wireOp",EDGE,"E46")])]});
            fillet(context, id + "F10", {"entities" : qUnion([Q0, Q1]), "radius" : 2 * mm, "tangentPropagation" : true, "allowEdgeOverflow" : false});
        }
        {
            var Q0;
            Q0=makeQuery(id+"F7.imprint","IMPRINT",FACE,{"disambiguationData":[TD([[makeQuery(id+"F7.imprint","IMPRINT",EDGE,{"derivedFrom":sQuery(id+"F7.wireOp",EDGE,"E35.0")}),1.0]])]});
            extrude(context, id + "F11", {"entities" : qUnion([Q0]), "operationType" : NewBodyOperationType.ADD, "oppositeDirection" : true, "depth" : 3 * mm, "offsetDistance" : 25 * mm});
        }
        {
            var Q0;
            {var subQ0=sQuery(id+"F7.wireOp",EDGE,"E61");Q0=makeQuery(id+"F7.imprint","IMPRINT",FACE,{"disambiguationData":[TD([[makeQuery(id+"F7.imprint","IMPRINT",EDGE,{"derivedFrom":subQ0}),1.0]])]});}
            extrude(context, id + "F12", {"entities" : qUnion([Q0]), "operationType" : NewBodyOperationType.ADD, "oppositeDirection" : true, "depth" : 2.2 * mm, "offsetDistance" : 25 * mm});
        }
    });
